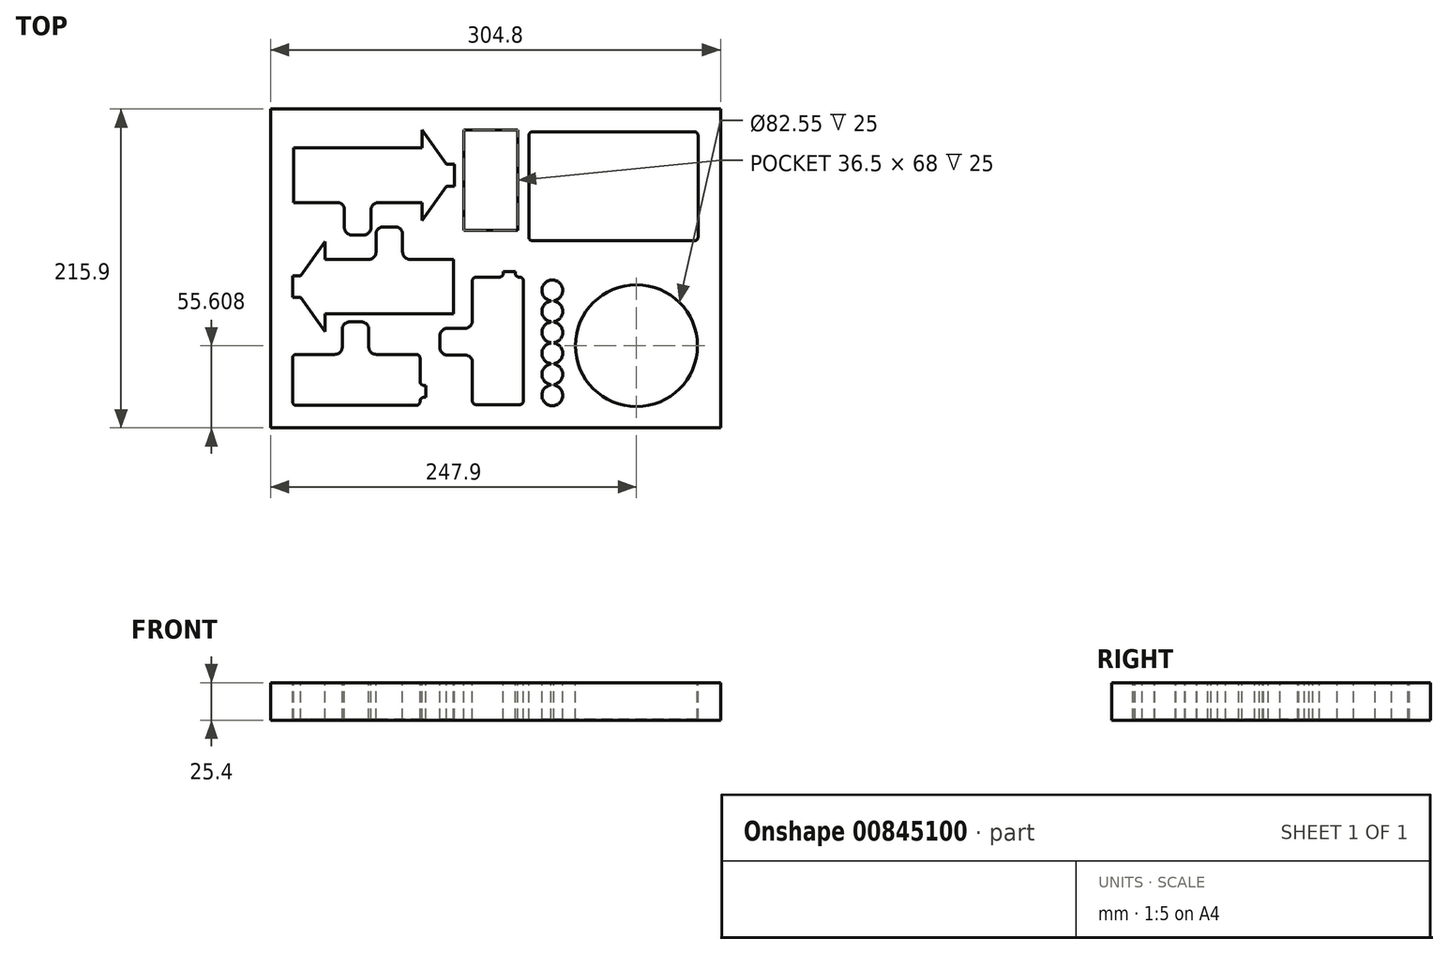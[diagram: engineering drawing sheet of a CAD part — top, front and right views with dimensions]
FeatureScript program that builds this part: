
annotation { "Feature Type Name" : "Feature", "Feature Type Description" : "" }
export const myFeature = defineFeature(function(context is Context, id is Id, definition is map)
    precondition{}
    {
        {
            var Q0;
            Q0=qCreatedBy(makeId("Top.planeOp"),FACE);
            var sketch = newSketch(context, id + "F0", { "sketchPlane" : qUnion([Q0])});
            skLineSegment(sketch, "E0.bottom", {"start": v(-135.3, 86.3) * mm, "end": v(169.5, 86.3) * mm});
            skLineSegment(sketch, "E0.top", {"start": v(-135.3, -129.6) * mm, "end": v(169.5, -129.6) * mm});
            skLineSegment(sketch, "E0.left", {"start": v(-135.3, 86.3) * mm, "end": v(-135.3, -129.6) * mm});
            skLineSegment(sketch, "E0.right", {"start": v(169.5, 86.3) * mm, "end": v(169.5, -129.6) * mm});
            skLineSegment(sketch, "E1.0", {"start": v(-120.3, 71.3) * mm, "end": v(-120.3, -114.6) * mm, "construction": true});
            skLineSegment(sketch, "E2.0", {"start": v(-120.3, 71.3) * mm, "end": v(154.5, 71.3) * mm, "construction": true});
            skLineSegment(sketch, "E3.0", {"start": v(154.5, 71.3) * mm, "end": v(154.5, -114.6) * mm, "construction": true});
            skLineSegment(sketch, "E4.0", {"start": v(-120.3, -114.6) * mm, "end": v(154.5, -114.6) * mm, "construction": true});
            skSolve(sketch);
        }
        {
            var Q0;
            Q0=makeQuery(id+"F0.imprint","IMPRINT",FACE,{"disambiguationData":[TD([[makeQuery(id+"F0.imprint","IMPRINT",EDGE,{"derivedFrom":sQuery(id+"F0.wireOp",EDGE,"E0.bottom")}),-1.0]])]});
            extrude(context, id + "F1", {"entities" : qUnion([Q0]), "depth" : 25.4 * mm, "offsetDistance" : 25.4 * mm});
        }
        {
            var Q0;
            Q0=makeQuery(id+"F1.opExtrude","CAP_FACE",FACE,{"disambiguationData":[OSD([sQuery(id+"F0.wireOp",EDGE,"E0.bottom"),sQuery(id+"F0.wireOp",EDGE,"E0.top"),sQuery(id+"F0.wireOp",EDGE,"E0.left"),sQuery(id+"F0.wireOp",EDGE,"E0.right")])],"isStart":false});
            var sketch = newSketch(context, id + "F2", { "sketchPlane" : qUnion([Q0])});
            skLineSegment(sketch, "E5.bottom", {"start": v(1.46, -111.39) * mm, "end": v(1.46, -85.28) * mm});
            skLineSegment(sketch, "E5.top", {"start": v(36, -111.39) * mm, "end": v(36, -30.1) * mm});
            skLineSegment(sketch, "E5.left", {"start": v(4, -113.93) * mm, "end": v(33.46, -113.93) * mm});
            skLineSegment(sketch, "E5.right", {"start": v(4, -27.57) * mm, "end": v(19.82, -27.57) * mm});
            skPoint(sketch, "E6.visualSharp", {"position": v(36, -113.93) * mm});
            skArc(sketch, "E6.filletArc", {"start": v(33.46, -113.93) * mm, "mid": v(35.26, -113.19) * mm, "end": v(36, -111.39) * mm});
            skPoint(sketch, "E7.visualSharp", {"position": v(36, -27.57) * mm});
            skArc(sketch, "E7.filletArc", {"start": v(36, -30.1) * mm, "mid": v(35.26, -28.31) * mm, "end": v(33.46, -27.57) * mm});
            skPoint(sketch, "E8.visualSharp", {"position": v(1.46, -27.57) * mm});
            skArc(sketch, "E8.filletArc", {"start": v(4, -27.57) * mm, "mid": v(2.2, -28.31) * mm, "end": v(1.46, -30.1) * mm});
            skPoint(sketch, "E9.visualSharp", {"position": v(1.46, -113.93) * mm});
            skArc(sketch, "E9.filletArc", {"start": v(1.46, -111.39) * mm, "mid": v(2.2, -113.19) * mm, "end": v(4, -113.93) * mm});
            skPoint(sketch, "E10", {"position": v(1.46, -70.75) * mm});
            skPoint(sketch, "E11", {"position": v(36, -70.75) * mm});
            skPoint(sketch, "E12", {"position": v(26.47, -27.57) * mm});
            skLineSegment(sketch, "E13.bottom", {"start": v(22.41, -24.98) * mm, "end": v(22.41, -23.76) * mm});
            skLineSegment(sketch, "E13.top", {"start": v(30.54, -24.98) * mm, "end": v(30.54, -23.76) * mm});
            skLineSegment(sketch, "E13.right", {"start": v(22.41, -23.76) * mm, "end": v(30.54, -23.76) * mm});
            skArc(sketch, "E14.filletArc", {"start": v(19.82, -27.57) * mm, "mid": v(21.65, -26.81) * mm, "end": v(22.41, -24.98) * mm});
            skLineSegment(sketch, "E15", {"start": v(33.46, -27.57) * mm, "end": v(33.13, -27.57) * mm});
            skPoint(sketch, "E16.visualSharp", {"position": v(30.54, -27.57) * mm});
            skArc(sketch, "E16.filletArc", {"start": v(30.54, -24.98) * mm, "mid": v(31.3, -26.81) * mm, "end": v(33.13, -27.57) * mm});
            skPoint(sketch, "E17", {"position": v(26.47, -23.76) * mm});
            skLineSegment(sketch, "E18.bottom", {"start": v(-20.54, -75.27) * mm, "end": v(-20.54, -67.24) * mm});
            skLineSegment(sketch, "E18.top", {"start": v(1.46, -71.26) * mm, "end": v(1.46, -70.75) * mm});
            skLineSegment(sketch, "E18.left", {"start": v(-15.54, -80.27) * mm, "end": v(-3.55, -80.27) * mm});
            skLineSegment(sketch, "E18.right", {"start": v(-15.54, -62.24) * mm, "end": v(-3.55, -62.24) * mm});
            skPoint(sketch, "E19", {"position": v(1.46, -71.26) * mm});
            skPoint(sketch, "E20.newPointA", {"position": v(1.46, -30.1) * mm});
            skArc(sketch, "E20.filletArc", {"start": v(1.46, -85.28) * mm, "mid": v(0, -81.74) * mm, "end": v(-3.55, -80.27) * mm});
            skPoint(sketch, "E21.visualSharp", {"position": v(-20.54, -80.27) * mm});
            skArc(sketch, "E21.filletArc", {"start": v(-20.54, -75.27) * mm, "mid": v(-19.07, -78.8) * mm, "end": v(-15.54, -80.27) * mm});
            skPoint(sketch, "E22.visualSharp", {"position": v(-20.54, -62.24) * mm});
            skArc(sketch, "E22.filletArc", {"start": v(-15.54, -62.24) * mm, "mid": v(-19.07, -63.7) * mm, "end": v(-20.54, -67.24) * mm});
            skLineSegment(sketch, "E23", {"start": v(1.46, -57.24) * mm, "end": v(1.46, -30.1) * mm});
            skPoint(sketch, "E24.visualSharp", {"position": v(1.46, -62.24) * mm});
            skArc(sketch, "E24.filletArc", {"start": v(-3.55, -62.24) * mm, "mid": v(0, -60.77) * mm, "end": v(1.46, -57.24) * mm});
            skPoint(sketch, "E25.orphan", {"position": v(1.46, -80.27) * mm});
            skSolve(sketch);
        }
        {
            var Q0;
            Q0=makeQuery(id+"F2.imprint","IMPRINT",FACE,{"disambiguationData":[TD([[makeQuery(id+"F2.imprint","IMPRINT",EDGE,{"derivedFrom":sQuery(id+"F2.wireOp",EDGE,"E5.bottom")}),1.0]])]});
            var sketch = newSketch(context, id + "F3", { "sketchPlane" : qUnion([Q0])});
            skPoint(sketch, "E26", {"position": v(-11.28, -35.62) * mm});
            skLineSegment(sketch, "E27.top", {"start": v(-11.28, -52.53) * mm, "end": v(-11.28, -15.53) * mm});
            skLineSegment(sketch, "E27.left", {"start": v(-98.28, -52.53) * mm, "end": v(-11.28, -52.53) * mm});
            skLineSegment(sketch, "E27.right", {"start": v(-98.28, -15.53) * mm, "end": v(-68.78, -15.53) * mm});
            skLineSegment(sketch, "E28.top", {"start": v(-98.28, -64.53) * mm, "end": v(-98.28, -52.53) * mm});
            skPoint(sketch, "E29", {"position": v(-98.28, -34.03) * mm});
            skLineSegment(sketch, "E30", {"start": v(-98.28, -64.53) * mm, "end": v(-114.94, -41.38) * mm});
            skLineSegment(sketch, "E31", {"start": v(-114.94, -26.68) * mm, "end": v(-98.28, -3.53) * mm});
            skLineSegment(sketch, "E32.trimOffspring", {"start": v(-98.28, -15.53) * mm, "end": v(-98.28, -3.53) * mm});
            skPoint(sketch, "E33.orphan", {"position": v(-120.23, -64.53) * mm});
            skPoint(sketch, "E28.bottom.end.orphan", {"position": v(-120.23, -3.53) * mm});
            skLineSegment(sketch, "E34.bottom", {"start": v(-120.23, -34.03) * mm, "end": v(-120.23, -26.68) * mm});
            skLineSegment(sketch, "E34.right", {"start": v(-120.23, -26.68) * mm, "end": v(-114.94, -26.68) * mm});
            skLineSegment(sketch, "E35.MirrorCS", {"start": v(-120.23, -41.38) * mm, "end": v(-114.94, -41.38) * mm});
            skLineSegment(sketch, "E36.MirrorCS", {"start": v(-120.23, -34.03) * mm, "end": v(-120.23, -41.38) * mm});
            skLineSegment(sketch, "E37.bottom", {"start": v(-58.78, 6.47) * mm, "end": v(-50.78, 6.47) * mm});
            skLineSegment(sketch, "E37.left", {"start": v(-63.78, 1.47) * mm, "end": v(-63.78, -10.53) * mm});
            skLineSegment(sketch, "E37.right", {"start": v(-45.78, 1.47) * mm, "end": v(-45.78, -10.53) * mm});
            skArc(sketch, "E38.filletArc", {"start": v(-68.78, -15.53) * mm, "mid": v(-65.25, -14.07) * mm, "end": v(-63.78, -10.53) * mm});
            skPoint(sketch, "E39.visualSharp", {"position": v(-63.78, 6.47) * mm});
            skArc(sketch, "E39.filletArc", {"start": v(-58.78, 6.47) * mm, "mid": v(-62.32, 5) * mm, "end": v(-63.78, 1.47) * mm});
            skPoint(sketch, "E40.visualSharp", {"position": v(-45.78, 6.47) * mm});
            skArc(sketch, "E40.filletArc", {"start": v(-45.78, 1.47) * mm, "mid": v(-47.25, 5) * mm, "end": v(-50.78, 6.47) * mm});
            skLineSegment(sketch, "E41", {"start": v(-40.78, -15.53) * mm, "end": v(-11.28, -15.53) * mm});
            skPoint(sketch, "E42.visualSharp", {"position": v(-45.78, -15.53) * mm});
            skArc(sketch, "E42.filletArc", {"start": v(-45.78, -10.53) * mm, "mid": v(-44.32, -14.07) * mm, "end": v(-40.78, -15.53) * mm});
            skSolve(sketch);
        }
        {
            var Q0;
            Q0=makeQuery(id+"F2.imprint","IMPRINT",FACE,{"disambiguationData":[TD([[makeQuery(id+"F2.imprint","IMPRINT",EDGE,{"derivedFrom":sQuery(id+"F2.wireOp",EDGE,"E5.bottom")}),1.0]])]});
            var sketch = newSketch(context, id + "F4", { "sketchPlane" : qUnion([Q0])});
            skLineSegment(sketch, "E43.bottom", {"start": v(42.28, 70.91) * mm, "end": v(151.75, 70.91) * mm});
            skLineSegment(sketch, "E43.top", {"start": v(42.28, -3) * mm, "end": v(151.75, -3) * mm});
            skLineSegment(sketch, "E43.left", {"start": v(39.74, 68.37) * mm, "end": v(39.74, -0.46) * mm});
            skLineSegment(sketch, "E43.right", {"start": v(154.3, 68.37) * mm, "end": v(154.3, -0.46) * mm});
            skPoint(sketch, "E44.visualSharp", {"position": v(39.74, 70.91) * mm});
            skArc(sketch, "E44.filletArc", {"start": v(42.28, 70.91) * mm, "mid": v(40.48, 70.17) * mm, "end": v(39.74, 68.37) * mm});
            skPoint(sketch, "E45.visualSharp", {"position": v(39.74, -3) * mm});
            skArc(sketch, "E45.filletArc", {"start": v(39.74, -0.46) * mm, "mid": v(40.48, -2.26) * mm, "end": v(42.28, -3) * mm});
            skPoint(sketch, "E46.visualSharp", {"position": v(154.3, -3) * mm});
            skArc(sketch, "E46.filletArc", {"start": v(151.75, -3) * mm, "mid": v(153.55, -2.26) * mm, "end": v(154.3, -0.46) * mm});
            skPoint(sketch, "E47.visualSharp", {"position": v(154.3, 70.91) * mm});
            skArc(sketch, "E47.filletArc", {"start": v(154.3, 68.37) * mm, "mid": v(153.55, 70.17) * mm, "end": v(151.75, 70.91) * mm});
            skSolve(sketch);
        }
        {
            var Q0;
            Q0=makeQuery(id+"F2.imprint","IMPRINT",FACE,{"disambiguationData":[TD([[makeQuery(id+"F2.imprint","IMPRINT",EDGE,{"derivedFrom":sQuery(id+"F2.wireOp",EDGE,"E5.bottom")}),1.0]])]});
            var sketch = newSketch(context, id + "F5", { "sketchPlane" : qUnion([Q0])});
            skCircle(sketch, "E48", {"center": v(112.6, -74) * mm, "radius": 41.27 * mm});
            skSolve(sketch);
        }
        {
            var Q0;
            Q0=makeQuery(id+"F2.imprint","IMPRINT",FACE,{"disambiguationData":[TD([[makeQuery(id+"F2.imprint","IMPRINT",EDGE,{"derivedFrom":sQuery(id+"F2.wireOp",EDGE,"E5.bottom")}),1.0]])]});
            var sketch = newSketch(context, id + "F6", { "sketchPlane" : qUnion([Q0])});
            skLineSegment(sketch, "E49.bottom", {"start": v(-117.8, -79.87) * mm, "end": v(-91.7, -79.87) * mm});
            skLineSegment(sketch, "E49.top", {"start": v(-117.8, -114.42) * mm, "end": v(-36.53, -114.42) * mm});
            skLineSegment(sketch, "E49.left", {"start": v(-120.35, -82.41) * mm, "end": v(-120.35, -111.88) * mm});
            skLineSegment(sketch, "E49.right", {"start": v(-33.99, -82.41) * mm, "end": v(-33.99, -98.24) * mm});
            skPoint(sketch, "E50.visualSharp", {"position": v(-120.35, -114.42) * mm});
            skArc(sketch, "E50.filletArc", {"start": v(-120.35, -111.88) * mm, "mid": v(-119.6, -113.67) * mm, "end": v(-117.8, -114.42) * mm});
            skPoint(sketch, "E51.visualSharp", {"position": v(-33.99, -114.42) * mm});
            skArc(sketch, "E51.filletArc", {"start": v(-36.53, -114.42) * mm, "mid": v(-34.73, -113.67) * mm, "end": v(-33.99, -111.88) * mm});
            skPoint(sketch, "E52.visualSharp", {"position": v(-33.99, -79.87) * mm});
            skArc(sketch, "E52.filletArc", {"start": v(-33.99, -82.41) * mm, "mid": v(-34.73, -80.62) * mm, "end": v(-36.53, -79.87) * mm});
            skPoint(sketch, "E53.visualSharp", {"position": v(-120.35, -79.87) * mm});
            skArc(sketch, "E53.filletArc", {"start": v(-117.8, -79.87) * mm, "mid": v(-119.6, -80.62) * mm, "end": v(-120.35, -82.41) * mm});
            skPoint(sketch, "E54", {"position": v(-77.17, -79.87) * mm});
            skPoint(sketch, "E55", {"position": v(-77.17, -114.42) * mm});
            skPoint(sketch, "E56", {"position": v(-33.99, -104.9) * mm});
            skLineSegment(sketch, "E57.bottom", {"start": v(-31.4, -100.83) * mm, "end": v(-30.18, -100.83) * mm});
            skLineSegment(sketch, "E57.top", {"start": v(-31.4, -108.96) * mm, "end": v(-30.18, -108.96) * mm});
            skLineSegment(sketch, "E57.right", {"start": v(-30.18, -100.83) * mm, "end": v(-30.18, -108.96) * mm});
            skArc(sketch, "E58.filletArc", {"start": v(-33.99, -98.24) * mm, "mid": v(-33.23, -100.07) * mm, "end": v(-31.4, -100.83) * mm});
            skLineSegment(sketch, "E59", {"start": v(-33.99, -111.88) * mm, "end": v(-33.99, -111.55) * mm});
            skPoint(sketch, "E60.visualSharp", {"position": v(-33.99, -108.96) * mm});
            skArc(sketch, "E60.filletArc", {"start": v(-31.4, -108.96) * mm, "mid": v(-33.23, -109.71) * mm, "end": v(-33.99, -111.55) * mm});
            skPoint(sketch, "E61", {"position": v(-30.18, -104.9) * mm});
            skLineSegment(sketch, "E62.bottom", {"start": v(-81.69, -57.88) * mm, "end": v(-73.66, -57.88) * mm});
            skLineSegment(sketch, "E62.top", {"start": v(-77.68, -79.87) * mm, "end": v(-77.17, -79.87) * mm});
            skLineSegment(sketch, "E62.left", {"start": v(-86.7, -62.88) * mm, "end": v(-86.7, -74.87) * mm});
            skLineSegment(sketch, "E62.right", {"start": v(-68.66, -62.88) * mm, "end": v(-68.66, -74.87) * mm});
            skPoint(sketch, "E63", {"position": v(-77.68, -79.87) * mm});
            skPoint(sketch, "E64.newPointA", {"position": v(-36.53, -79.87) * mm});
            skArc(sketch, "E64.filletArc", {"start": v(-91.7, -79.87) * mm, "mid": v(-88.16, -78.4) * mm, "end": v(-86.7, -74.87) * mm});
            skPoint(sketch, "E65.visualSharp", {"position": v(-86.7, -57.88) * mm});
            skArc(sketch, "E65.filletArc", {"start": v(-81.69, -57.88) * mm, "mid": v(-85.23, -59.34) * mm, "end": v(-86.7, -62.88) * mm});
            skPoint(sketch, "E66.visualSharp", {"position": v(-68.66, -57.88) * mm});
            skArc(sketch, "E66.filletArc", {"start": v(-68.66, -62.88) * mm, "mid": v(-70.12, -59.34) * mm, "end": v(-73.66, -57.88) * mm});
            skLineSegment(sketch, "E67", {"start": v(-63.65, -79.87) * mm, "end": v(-36.53, -79.87) * mm});
            skPoint(sketch, "E68.visualSharp", {"position": v(-68.66, -79.87) * mm});
            skArc(sketch, "E68.filletArc", {"start": v(-68.66, -74.87) * mm, "mid": v(-67.2, -78.4) * mm, "end": v(-63.65, -79.87) * mm});
            skPoint(sketch, "E69.orphan", {"position": v(-86.7, -79.87) * mm});
            skSolve(sketch);
        }
        {
            var Q0;
            Q0=makeQuery(id+"F2.imprint","IMPRINT",FACE,{"disambiguationData":[TD([[makeQuery(id+"F2.imprint","IMPRINT",EDGE,{"derivedFrom":sQuery(id+"F2.wireOp",EDGE,"E5.bottom")}),1.0]])]});
            var sketch = newSketch(context, id + "F7", { "sketchPlane" : qUnion([Q0])});
            skLineSegment(sketch, "E70.direction1", {"start": v(55.58, -36.56) * mm, "end": v(69.68, -36.56) * mm, "construction": true});
            skLineSegment(sketch, "E70.direction2", {"start": v(55.58, -36.56) * mm, "end": v(55.58, -39.37) * mm, "construction": true});
            skArc(sketch, "E71", {"start": v(56.58, -43.54) * mm, "mid": v(55.58, -29.5) * mm, "end": v(54.58, -43.54) * mm});
            skArc(sketch, "E72.0.1.0", {"start": v(54.58, -43.78) * mm, "mid": v(48.53, -50.76) * mm, "end": v(54.58, -57.74) * mm});
            skArc(sketch, "E72.0.2.0", {"start": v(54.58, -57.98) * mm, "mid": v(48.53, -64.96) * mm, "end": v(54.58, -71.94) * mm});
            skArc(sketch, "E72.0.3.0", {"start": v(54.58, -72.18) * mm, "mid": v(48.53, -79.16) * mm, "end": v(54.58, -86.14) * mm});
            skArc(sketch, "E72.0.4.0", {"start": v(54.58, -86.38) * mm, "mid": v(48.53, -93.36) * mm, "end": v(54.58, -100.34) * mm});
            skArc(sketch, "E72.0.5.0", {"start": v(54.58, -100.58) * mm, "mid": v(55.58, -114.6) * mm, "end": v(56.58, -100.58) * mm});
            skLineSegment(sketch, "E72.direction1", {"start": v(55.58, -36.56) * mm, "end": v(80.58, -36.56) * mm, "construction": true});
            skLineSegment(sketch, "E72.direction2", {"start": v(55.58, -36.56) * mm, "end": v(55.58, -50.76) * mm, "construction": true});
            skLineSegment(sketch, "E73.bottom", {"start": v(55.58, -36.56) * mm, "end": v(56.58, -36.56) * mm});
            skLineSegment(sketch, "E73.right", {"start": v(56.58, -43.54) * mm, "end": v(56.58, -43.78) * mm});
            skLineSegment(sketch, "E74.MirrorCS", {"start": v(54.58, -43.54) * mm, "end": v(54.58, -43.78) * mm});
            skArc(sketch, "E75.trimOffspring", {"start": v(56.58, -57.74) * mm, "mid": v(62.63, -50.76) * mm, "end": v(56.58, -43.78) * mm});
            skArc(sketch, "E76.trimOffspring", {"start": v(56.58, -71.94) * mm, "mid": v(62.63, -64.96) * mm, "end": v(56.58, -57.98) * mm});
            skArc(sketch, "E77.trimOffspring", {"start": v(56.58, -86.14) * mm, "mid": v(62.63, -79.16) * mm, "end": v(56.58, -72.18) * mm});
            skArc(sketch, "E78.trimOffspring", {"start": v(56.58, -100.34) * mm, "mid": v(62.63, -93.36) * mm, "end": v(56.58, -86.38) * mm});
            skPoint(sketch, "E79.orphan", {"position": v(54.58, -107.68) * mm});
            skPoint(sketch, "E80.orphan", {"position": v(56.58, -107.68) * mm});
            skLineSegment(sketch, "E81.trimOffspring", {"start": v(56.58, -100.34) * mm, "end": v(56.58, -100.58) * mm});
            skLineSegment(sketch, "E82.trimOffspring", {"start": v(54.58, -100.34) * mm, "end": v(54.58, -100.58) * mm});
            skLineSegment(sketch, "E83.trimOffspring", {"start": v(54.58, -86.14) * mm, "end": v(54.58, -86.38) * mm});
            skLineSegment(sketch, "E84.trimOffspring", {"start": v(56.58, -86.14) * mm, "end": v(56.58, -86.38) * mm});
            skLineSegment(sketch, "E85.trimOffspring", {"start": v(54.58, -71.94) * mm, "end": v(54.58, -72.18) * mm});
            skLineSegment(sketch, "E86.trimOffspring", {"start": v(56.58, -71.94) * mm, "end": v(56.58, -72.18) * mm});
            skLineSegment(sketch, "E87.trimOffspring", {"start": v(54.58, -57.74) * mm, "end": v(54.58, -57.98) * mm});
            skLineSegment(sketch, "E88.trimOffspring", {"start": v(56.58, -57.74) * mm, "end": v(56.58, -57.98) * mm});
            skPoint(sketch, "E89.orphan", {"position": v(54.58, -36.56) * mm});
            skSolve(sketch);
        }
        {
            var Q0;
            Q0=makeQuery(id+"F2.imprint","IMPRINT",FACE,{"disambiguationData":[TD([[makeQuery(id+"F2.imprint","IMPRINT",EDGE,{"derivedFrom":sQuery(id+"F2.wireOp",EDGE,"E5.bottom")}),1.0]])]});
            var sketch = newSketch(context, id + "F8", { "sketchPlane" : qUnion([Q0])});
            skLineSegment(sketch, "E90.bottom", {"start": v(-4.35, 72) * mm, "end": v(32.15, 72) * mm});
            skLineSegment(sketch, "E90.top", {"start": v(-4.35, 4) * mm, "end": v(32.15, 4) * mm});
            skLineSegment(sketch, "E90.left", {"start": v(-4.35, 72) * mm, "end": v(-4.35, 4) * mm});
            skLineSegment(sketch, "E90.right", {"start": v(32.15, 72) * mm, "end": v(32.15, 4) * mm});
            skSolve(sketch);
        }
        {
            var Q0;
            Q0=makeQuery(id+"F3.imprint","IMPRINT",FACE,{"disambiguationData":[TD([[makeQuery(id+"F3.imprint","IMPRINT",EDGE,{"derivedFrom":sQuery(id+"F3.wireOp",EDGE,"E27.top")}),-1.0]])]});
            var sketch = newSketch(context, id + "F9", { "sketchPlane" : qUnion([Q0])});
            skPoint(sketch, "E91", {"position": v(-119.68, 43.05) * mm});
            skLineSegment(sketch, "E92.top", {"start": v(-119.68, 59.96) * mm, "end": v(-119.68, 22.96) * mm});
            skLineSegment(sketch, "E92.left", {"start": v(-32.68, 59.96) * mm, "end": v(-119.68, 59.96) * mm});
            skLineSegment(sketch, "E92.right", {"start": v(-32.68, 22.96) * mm, "end": v(-62.18, 22.96) * mm});
            skLineSegment(sketch, "E93.top", {"start": v(-32.68, 71.96) * mm, "end": v(-32.68, 59.96) * mm});
            skPoint(sketch, "E94", {"position": v(-32.68, 41.46) * mm});
            skLineSegment(sketch, "E95", {"start": v(-32.68, 71.96) * mm, "end": v(-16.02, 48.8) * mm});
            skLineSegment(sketch, "E96", {"start": v(-16.02, 34.1) * mm, "end": v(-32.68, 10.96) * mm});
            skLineSegment(sketch, "E97.trimOffspring", {"start": v(-32.68, 22.96) * mm, "end": v(-32.68, 10.96) * mm});
            skPoint(sketch, "E98.orphan", {"position": v(-10.73, 71.96) * mm});
            skPoint(sketch, "E93.bottom.end.orphan", {"position": v(-10.73, 10.96) * mm});
            skLineSegment(sketch, "E99.bottom", {"start": v(-10.73, 41.46) * mm, "end": v(-10.73, 34.1) * mm});
            skLineSegment(sketch, "E99.right", {"start": v(-10.73, 34.1) * mm, "end": v(-16.02, 34.1) * mm});
            skLineSegment(sketch, "E100.MirrorCS", {"start": v(-10.73, 48.8) * mm, "end": v(-16.02, 48.8) * mm});
            skLineSegment(sketch, "E101.MirrorCS", {"start": v(-10.73, 41.46) * mm, "end": v(-10.73, 48.8) * mm});
            skLineSegment(sketch, "E102.bottom", {"start": v(-72.18, 0.96) * mm, "end": v(-80.18, 0.96) * mm});
            skLineSegment(sketch, "E102.left", {"start": v(-67.18, 5.96) * mm, "end": v(-67.18, 17.96) * mm});
            skLineSegment(sketch, "E102.right", {"start": v(-85.18, 5.96) * mm, "end": v(-85.18, 17.96) * mm});
            skArc(sketch, "E103.filletArc", {"start": v(-62.18, 22.96) * mm, "mid": v(-65.71, 21.5) * mm, "end": v(-67.18, 17.96) * mm});
            skPoint(sketch, "E104.visualSharp", {"position": v(-67.18, 0.96) * mm});
            skArc(sketch, "E104.filletArc", {"start": v(-72.18, 0.96) * mm, "mid": v(-68.64, 2.42) * mm, "end": v(-67.18, 5.96) * mm});
            skPoint(sketch, "E105.visualSharp", {"position": v(-85.18, 0.96) * mm});
            skArc(sketch, "E105.filletArc", {"start": v(-85.18, 5.96) * mm, "mid": v(-83.71, 2.42) * mm, "end": v(-80.18, 0.96) * mm});
            skLineSegment(sketch, "E106", {"start": v(-90.18, 22.96) * mm, "end": v(-119.68, 22.96) * mm});
            skPoint(sketch, "E107.visualSharp", {"position": v(-85.18, 22.96) * mm});
            skArc(sketch, "E107.filletArc", {"start": v(-85.18, 17.96) * mm, "mid": v(-86.64, 21.5) * mm, "end": v(-90.18, 22.96) * mm});
            skSolve(sketch);
        }
        {
            var Q0;
            Q0 = qSketchRegion(id + "F0", true);
            var Q1;
            Q1 = qSketchRegion(id + "F2", true);
            var Q2;
            Q2 = qSketchRegion(id + "F3", true);
            var Q3;
            Q3 = qSketchRegion(id + "F4", true);
            var Q4;
            Q4 = qSketchRegion(id + "F5", true);
            var Q5;
            Q5 = qSketchRegion(id + "F6", true);
            var Q6;
            Q6 = qSketchRegion(id + "F7", true);
            var Q7;
            Q7 = qSketchRegion(id + "F8", true);
            var Q8;
            Q8 = qSketchRegion(id + "F9", true);
            extrude(context, id + "F10", {"entities" : qUnion([Q0, Q1, Q2, Q3, Q4, Q5, Q6, Q7, Q8]), "operationType" : NewBodyOperationType.REMOVE, "oppositeDirection" : true, "depth" : 25 * mm, "offsetDistance" : 25 * mm});
        }
    });
